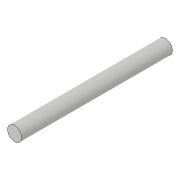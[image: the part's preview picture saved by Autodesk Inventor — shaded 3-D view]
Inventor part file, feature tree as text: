
AUTODESK INVENTOR PART (.ipt)
format: ipt  version: 2018.3 (Build 223284000, 284)  size: 70,656 bytes
history: native  units: in
note: dims shown in document units (in); Inventor stores cm internally (conversion verified against a paired STEP export)
features: extrude x1, sketch x1
ambient origin geometry x8: Origin, YZ Plane, XZ Plane, XY Plane, X Axis, Y Axis, Z Axis, Center Point
bodies: Solid1 (feature_tree)
feature tree (2):
  extrude  "Extrusion1"  Depth=8.0in TaperAngle=0.0deg
  sketch  "Sketch1"  dims[d0=0.75in d1=8.0in d2=0.0in]
